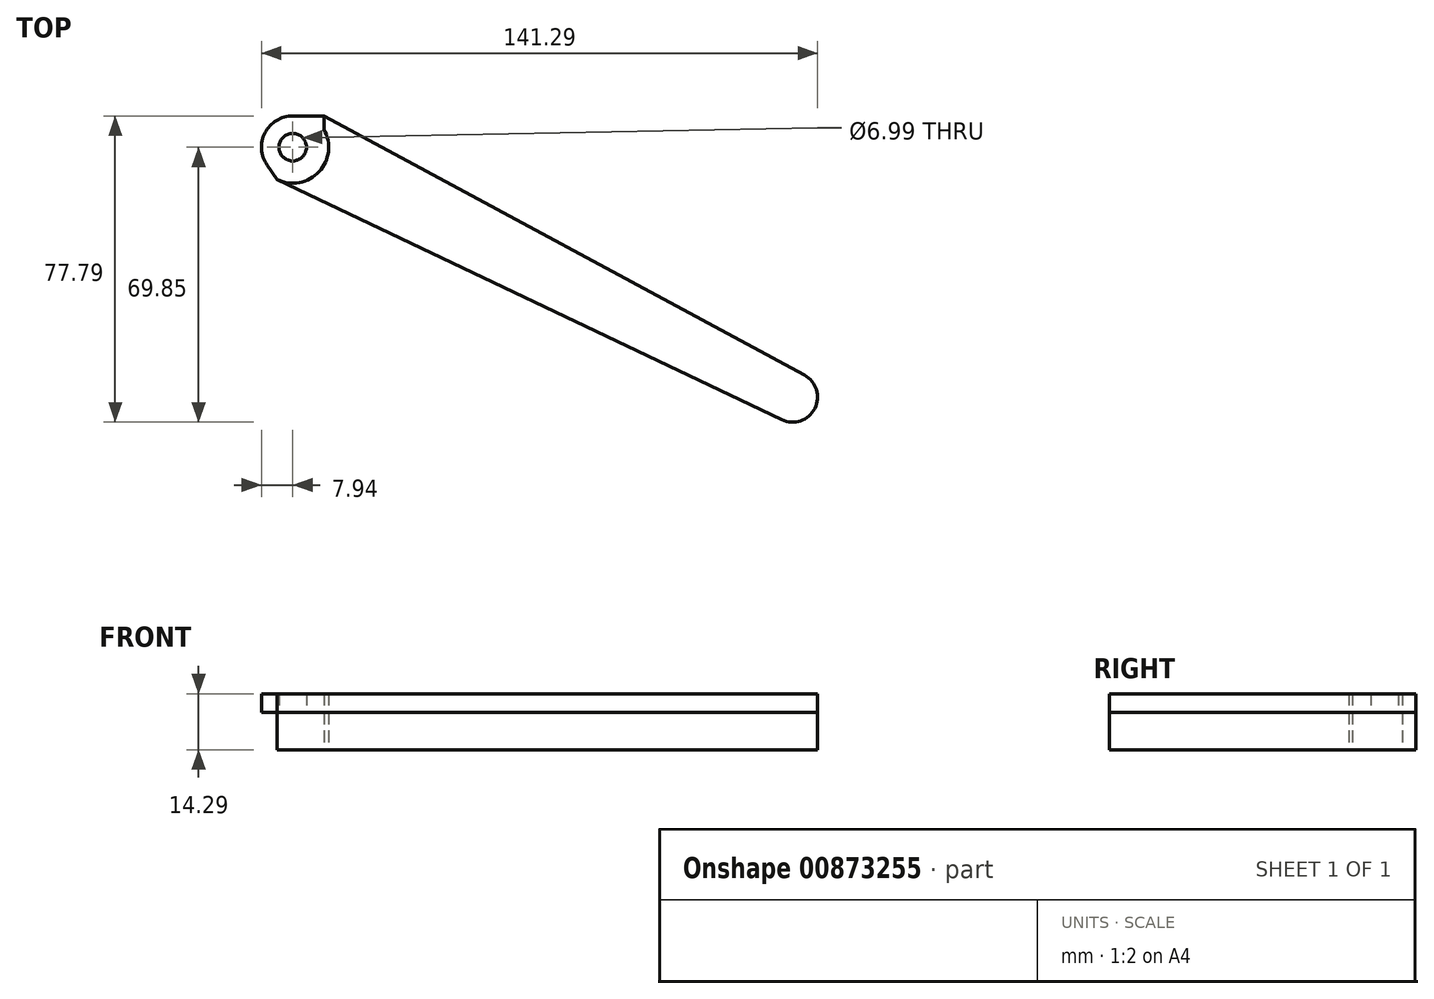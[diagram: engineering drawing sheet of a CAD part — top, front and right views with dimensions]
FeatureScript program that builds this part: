
annotation { "Feature Type Name" : "Feature", "Feature Type Description" : "" }
export const myFeature = defineFeature(function(context is Context, id is Id, definition is map)
    precondition{}
    {
        {
            var Q0;
            Q0=qCreatedBy(makeId("Top.planeOp"),FACE);
            var sketch = newSketch(context, id + "F0", { "sketchPlane" : qUnion([Q0])});
            skCircle(sketch, "E0", {"center": v(0, 0) * mm, "radius": 7.94 * mm});
            skLineSegment(sketch, "E1.bottom", {"start": v(-7.94, 0) * mm, "end": v(7.94, 0) * mm});
            skLineSegment(sketch, "E1.top", {"start": v(-7.94, 7.94) * mm, "end": v(7.94, 7.94) * mm});
            skLineSegment(sketch, "E1.left", {"start": v(-7.94, 0) * mm, "end": v(-7.94, 7.94) * mm});
            skLineSegment(sketch, "E1.right", {"start": v(7.94, 0) * mm, "end": v(7.94, 7.94) * mm});
            skLineSegment(sketch, "E2", {"start": v(7.94, 7.94) * mm, "end": v(130.01, -57.91) * mm});
            skArc(sketch, "E3", {"start": v(130.01, -57.91) * mm, "mid": v(132.65, -66.4) * mm, "end": v(124.22, -69.21) * mm});
            skLineSegment(sketch, "E4", {"start": v(124.22, -69.21) * mm, "end": v(-3.92, -8.24) * mm});
            skCircle(sketch, "E5", {"center": v(0, 0) * mm, "radius": 9.13 * mm});
            skSolve(sketch);
        }
        {
            var Q0;
            {var subQ1=sQuery(id+"F0.wireOp",EDGE,"E2");Q0=makeQuery(id+"F0.imprint","IMPRINT",FACE,{"disambiguationData":[TD([[makeQuery(id+"F0.imprint","IMPRINT",EDGE,{"derivedFrom":subQ1}),-1.0]])]});}
            extrude(context, id + "F1", {"entities" : qUnion([Q0]), "depth" : 9.52 * mm, "offsetDistance" : 25.4 * mm});
        }
        {
            var Q0;
            Q0=makeQuery(id+"F1.opExtrude","CAP_FACE",FACE,{"disambiguationData":[OSD([sQuery(id+"F0.wireOp",EDGE,"E1.right"),sQuery(id+"F0.wireOp",EDGE,"E2"),sQuery(id+"F0.wireOp",EDGE,"E3"),sQuery(id+"F0.wireOp",EDGE,"E4"),sQuery(id+"F0.wireOp",EDGE,"E5")])],"isStart":false});
            var sketch = newSketch(context, id + "F2", { "sketchPlane" : qUnion([Q0])});
            skCircle(sketch, "E6", {"center": v(0, 0) * mm, "radius": 7.94 * mm});
            skLineSegment(sketch, "E7", {"start": v(7.94, 7.94) * mm, "end": v(0, 7.94) * mm});
            skLineSegment(sketch, "E8", {"start": v(-3.92, -8.24) * mm, "end": v(-6.5, -4.55) * mm});
            skCircle(sketch, "E9", {"center": v(0, 0) * mm, "radius": 3.5 * mm});
            skSolve(sketch);
        }
        {
            var Q0;
            Q0=makeQuery(id+"F2.imprint","IMPRINT",FACE,{"disambiguationData":[TD([[makeQuery(id+"F2.imprint","IMPRINT",EDGE,{"derivedFrom":sQuery(id+"F2.wireOp",EDGE,"E9")}),-1.0]])]});
            var Q1;
            {var subQ1=sQuery(id+"F2.wireOp",EDGE,"E7");Q1=makeQuery(id+"F2.imprint","IMPRINT",FACE,{"disambiguationData":[TD([[makeQuery(id+"F2.imprint","IMPRINT",EDGE,{"derivedFrom":subQ1}),1.0]])]});}
            extrude(context, id + "F3", {"entities" : qUnion([Q0, Q1]), "depth" : 4.76 * mm, "offsetDistance" : 25.4 * mm});
        }
        {
            var Q0;
            Q0=makeQuery(id+"F1.opExtrude","CAP_FACE",FACE,{"disambiguationData":[OSD([sQuery(id+"F0.wireOp",EDGE,"E1.right"),sQuery(id+"F0.wireOp",EDGE,"E2"),sQuery(id+"F0.wireOp",EDGE,"E3"),sQuery(id+"F0.wireOp",EDGE,"E4"),sQuery(id+"F0.wireOp",EDGE,"E5")])],"isStart":false});
            var sketch = newSketch(context, id + "F4", { "sketchPlane" : qUnion([Q0])});
            skLineSegment(sketch, "E10", {"start": v(9.47, -5.7) * mm, "end": v(15.16, -10.43) * mm});
            skSolve(sketch);
        }
        {
            var Q0;
            Q0=makeQuery(id+"F4.imprint","IMPRINT",FACE,{"disambiguationData":[TD([[makeQuery(id+"F4.imprint","IMPRINT",EDGE,{"derivedFrom":makeQuery(id+"F1.opExtrude","CAP_EDGE",EDGE,{"disambiguationData":[OSD([sQuery(id+"F0.wireOp",EDGE,"E1.right")])],"isStart":false})}),-1.0]])]});
            extrude(context, id + "F5", {"entities" : qUnion([Q0]), "depth" : 4.76 * mm, "offsetDistance" : 25.4 * mm});
        }
    });
